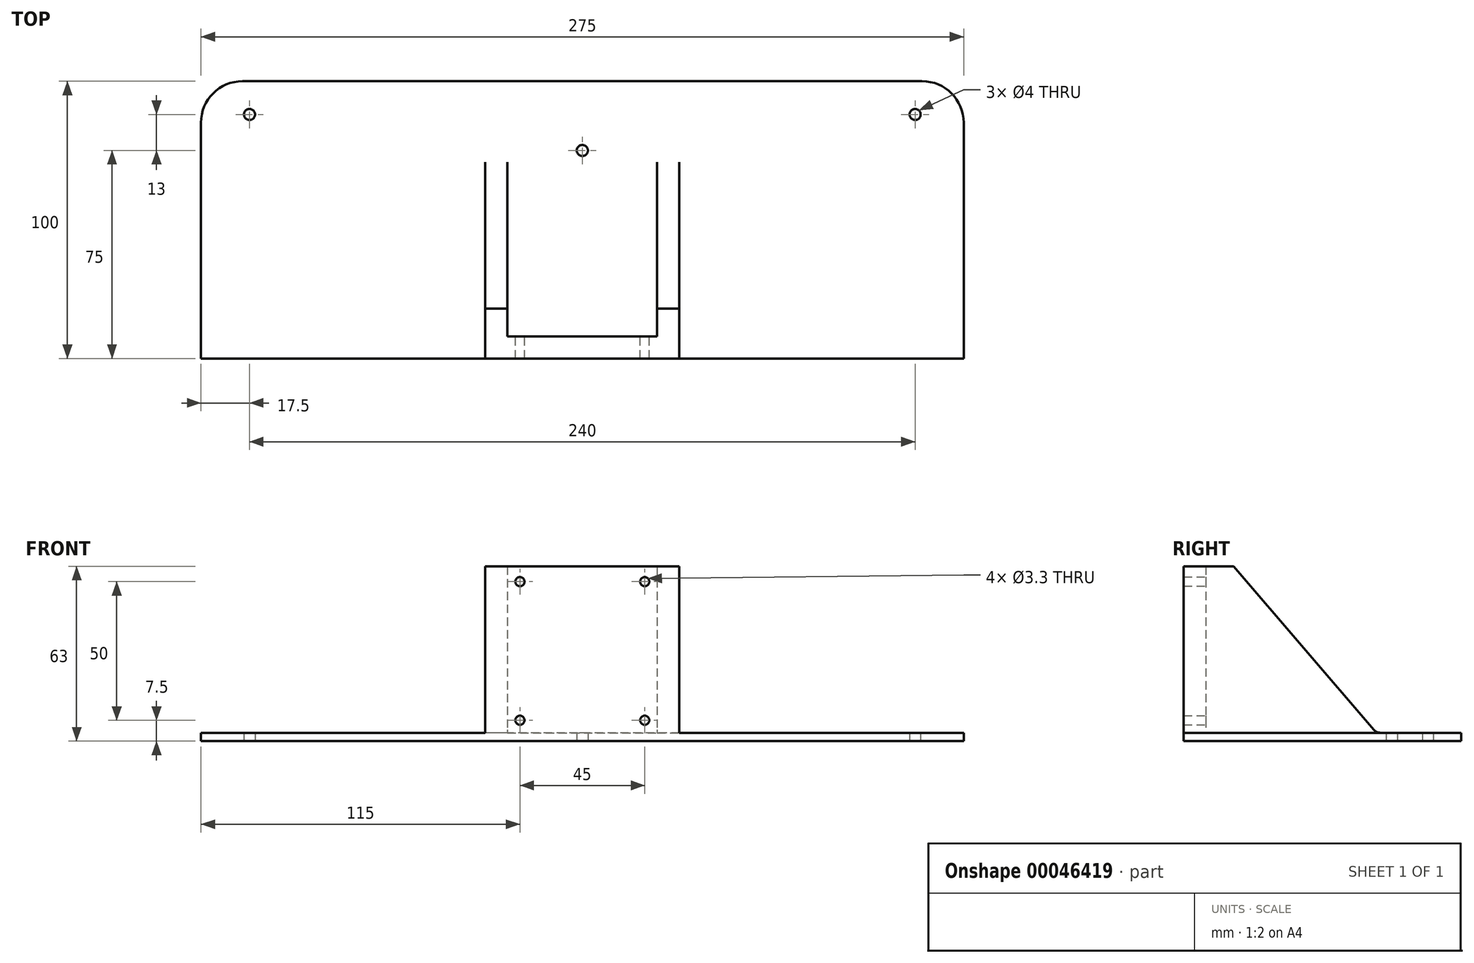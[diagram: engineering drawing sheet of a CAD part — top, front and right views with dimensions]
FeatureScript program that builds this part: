
annotation { "Feature Type Name" : "Feature", "Feature Type Description" : "" }
export const myFeature = defineFeature(function(context is Context, id is Id, definition is map)
    precondition{}
    {
        {
            var Q0;
            Q0=qCreatedBy(makeId("Top.planeOp"),FACE);
            var sketch = newSketch(context, id + "F0", { "sketchPlane" : qUnion([Q0])});
            skLineSegment(sketch, "E0.bottom", {"start": v(137.5, -50) * mm, "end": v(-137.5, -50) * mm});
            skLineSegment(sketch, "E0.top", {"start": v(122.5, 50) * mm, "end": v(-122.5, 50) * mm});
            skLineSegment(sketch, "E0.left", {"start": v(137.5, -50) * mm, "end": v(137.5, 35) * mm});
            skLineSegment(sketch, "E0.right", {"start": v(-137.5, -50) * mm, "end": v(-137.5, 35) * mm});
            skPoint(sketch, "E0.middle", {"position": v(0, 0) * mm});
            skPoint(sketch, "E1.visualSharp", {"position": v(-137.5, 50) * mm});
            skArc(sketch, "E1.filletArc", {"start": v(-122.5, 50) * mm, "mid": v(-133.1, 45.6) * mm, "end": v(-137.5, 35) * mm});
            skPoint(sketch, "E2.visualSharp", {"position": v(137.5, 50) * mm});
            skArc(sketch, "E2.filletArc", {"start": v(137.5, 35) * mm, "mid": v(133.1, 45.6) * mm, "end": v(122.5, 50) * mm});
            skPoint(sketch, "E3", {"position": v(0, 25) * mm});
            skPoint(sketch, "E4", {"position": v(-120, 38) * mm});
            skCircle(sketch, "E5", {"center": v(-120, 38) * mm, "radius": 2 * mm});
            skCircle(sketch, "E6", {"center": v(0, 25) * mm, "radius": 2 * mm});
            skCircle(sketch, "E7.MirrorC", {"center": v(120, 38) * mm, "radius": 2 * mm});
            skSolve(sketch);
        }
        {
            var Q0;
            Q0=makeQuery(id+"F0.imprint","IMPRINT",FACE,{"disambiguationData":[TD([[makeQuery(id+"F0.imprint","IMPRINT",EDGE,{"derivedFrom":sQuery(id+"F0.wireOp",EDGE,"E0.bottom")}),-1.0]])]});
            extrude(context, id + "F1", {"entities" : qUnion([Q0]), "depth" : 3 * mm, "offsetDistance" : 25 * mm});
        }
        {
            var Q0;
            Q0=makeQuery(id+"F1.opExtrude","CAP_FACE",FACE,{"disambiguationData":[OSD([sQuery(id+"F0.wireOp",EDGE,"E0.bottom"),sQuery(id+"F0.wireOp",EDGE,"E0.top"),sQuery(id+"F0.wireOp",EDGE,"E0.left"),sQuery(id+"F0.wireOp",EDGE,"E0.right"),sQuery(id+"F0.wireOp",EDGE,"E1.filletArc"),sQuery(id+"F0.wireOp",EDGE,"E2.filletArc"),sQuery(id+"F0.wireOp",EDGE,"E5"),sQuery(id+"F0.wireOp",EDGE,"E6"),sQuery(id+"F0.wireOp",EDGE,"E7.MirrorC")])],"isStart":false});
            var sketch = newSketch(context, id + "F2", { "sketchPlane" : qUnion([Q0])});
            skLineSegment(sketch, "E8.bottom", {"start": v(-35, -50) * mm, "end": v(35, -50) * mm});
            skLineSegment(sketch, "E8.top", {"start": v(-35, -42) * mm, "end": v(35, -42) * mm});
            skLineSegment(sketch, "E8.left", {"start": v(-35, -50) * mm, "end": v(-35, -42) * mm});
            skLineSegment(sketch, "E8.right", {"start": v(35, -50) * mm, "end": v(35, -42) * mm});
            skLineSegment(sketch, "E9.bottom", {"start": v(-35, -42) * mm, "end": v(-27, -42) * mm});
            skLineSegment(sketch, "E9.left", {"start": v(-35, -42) * mm, "end": v(-35, 28) * mm});
            skLineSegment(sketch, "E10.MirrorCS", {"start": v(35, -42) * mm, "end": v(35, 28) * mm});
            skLineSegment(sketch, "E11", {"start": v(-35, 28) * mm, "end": v(-27, 28) * mm});
            skLineSegment(sketch, "E12", {"start": v(-27, 28) * mm, "end": v(-27, -42) * mm});
            skLineSegment(sketch, "E13.MirrorCS", {"start": v(35, 28) * mm, "end": v(27, 28) * mm});
            skLineSegment(sketch, "E14.MirrorCS", {"start": v(27, 28) * mm, "end": v(27, -42) * mm});
            skSolve(sketch);
        }
        {
            var Q0;
            Q0=makeQuery(id+"F2.imprint","IMPRINT",FACE,{"disambiguationData":[TD([[makeQuery(id+"F2.imprint","IMPRINT",EDGE,{"derivedFrom":sQuery(id+"F2.wireOp",EDGE,"E8.bottom")}),-1.0]])]});
            var Q1;
            {var subQ2=sQuery(id+"F2.wireOp",EDGE,"E9.left");Q1=makeQuery(id+"F2.imprint","IMPRINT",FACE,{"disambiguationData":[TD([[makeQuery(id+"F2.imprint","IMPRINT",EDGE,{"derivedFrom":subQ2}),-1.0]])]});}
            var Q2;
            {var subQ0=sQuery(id+"F2.wireOp",EDGE,"E10.MirrorCS");Q2=makeQuery(id+"F2.imprint","IMPRINT",FACE,{"disambiguationData":[TD([[makeQuery(id+"F2.imprint","IMPRINT",EDGE,{"derivedFrom":subQ0}),1.0]])]});}
            extrude(context, id + "F3", {"entities" : qUnion([Q0, Q1, Q2]), "operationType" : NewBodyOperationType.ADD, "depth" : 60 * mm, "offsetDistance" : 25 * mm});
        }
        {
            var Q0;
            Q0=makeQuery(id+"F3.opExtrude","CAP_EDGE",EDGE,{"disambiguationData":[OSD([sQuery(id+"F2.wireOp",EDGE,"E11")])],"isStart":false});
            var Q1;
            Q1=makeQuery(id+"F3.opExtrude","CAP_EDGE",EDGE,{"disambiguationData":[OSD([sQuery(id+"F2.wireOp",EDGE,"E13.MirrorCS")])],"isStart":false});
            chamfer(context, id + "F4", {"entities" : qUnion([Q0, Q1]), "chamferType" : ChamferType.TWO_OFFSETS, "width1" : 60 * mm, "oppositeDirection" : false, "width2" : 70 * mm, "tangentPropagation" : true});
        }
        {
            var Q0;
            Q0=makeQuery(id+"F3.opExtrude","CAP_EDGE",EDGE,{"disambiguationData":[OSD([sQuery(id+"F2.wireOp",EDGE,"E8.right"),sQuery(id+"F2.wireOp",EDGE,"E10.MirrorCS")])],"isStart":true});
            var Q1;
            Q1=makeQuery(id+"F3.opExtrude","CAP_EDGE",EDGE,{"disambiguationData":[OSD([sQuery(id+"F2.wireOp",EDGE,"E8.left"),sQuery(id+"F2.wireOp",EDGE,"E9.left")])],"isStart":true});
            var Q2;
            Q2=makeQuery(id+"F3.opExtrude","CAP_EDGE",EDGE,{"disambiguationData":[OSD([sQuery(id+"F2.wireOp",EDGE,"E12")])],"isStart":true});
            var Q3;
            Q3=makeQuery(id+"F3.opExtrude","CAP_EDGE",EDGE,{"disambiguationData":[OSD([sQuery(id+"F2.wireOp",EDGE,"E8.top")])],"isStart":true});
            var Q4;
            Q4=makeQuery(id+"F3.opExtrude","CAP_EDGE",EDGE,{"disambiguationData":[OSD([sQuery(id+"F2.wireOp",EDGE,"E14.MirrorCS")])],"isStart":true});
            var Q5;
            Q5=makeQuery(id+"F4.opChamfer","BLEND_EDGE",EDGE,{"blendedFrom":[makeQuery(id+"F3.opExtrude","CAP_EDGE",EDGE,{"disambiguationData":[OSD([sQuery(id+"F2.wireOp",EDGE,"E11")])],"isStart":false}),makeQuery(id+"F1.opExtrude","CAP_FACE",FACE,{"disambiguationData":[OSD([sQuery(id+"F0.wireOp",EDGE,"E0.bottom"),sQuery(id+"F0.wireOp",EDGE,"E0.top"),sQuery(id+"F0.wireOp",EDGE,"E0.left"),sQuery(id+"F0.wireOp",EDGE,"E0.right"),sQuery(id+"F0.wireOp",EDGE,"E1.filletArc"),sQuery(id+"F0.wireOp",EDGE,"E2.filletArc"),sQuery(id+"F0.wireOp",EDGE,"E5"),sQuery(id+"F0.wireOp",EDGE,"E6"),sQuery(id+"F0.wireOp",EDGE,"E7.MirrorC")])],"isStart":false})],"blendedInto":[makeQuery(id+"F1.opExtrude","CAP_FACE",FACE,{"disambiguationData":[OSD([sQuery(id+"F0.wireOp",EDGE,"E0.bottom"),sQuery(id+"F0.wireOp",EDGE,"E0.top"),sQuery(id+"F0.wireOp",EDGE,"E0.left"),sQuery(id+"F0.wireOp",EDGE,"E0.right"),sQuery(id+"F0.wireOp",EDGE,"E1.filletArc"),sQuery(id+"F0.wireOp",EDGE,"E2.filletArc"),sQuery(id+"F0.wireOp",EDGE,"E5"),sQuery(id+"F0.wireOp",EDGE,"E6"),sQuery(id+"F0.wireOp",EDGE,"E7.MirrorC")])],"isStart":false})]});
            var Q6;
            Q6=makeQuery(id+"F4.opChamfer","BLEND_EDGE",EDGE,{"blendedFrom":[makeQuery(id+"F3.opExtrude","CAP_EDGE",EDGE,{"disambiguationData":[OSD([sQuery(id+"F2.wireOp",EDGE,"E13.MirrorCS")])],"isStart":false}),makeQuery(id+"F1.opExtrude","CAP_FACE",FACE,{"disambiguationData":[OSD([sQuery(id+"F0.wireOp",EDGE,"E0.bottom"),sQuery(id+"F0.wireOp",EDGE,"E0.top"),sQuery(id+"F0.wireOp",EDGE,"E0.left"),sQuery(id+"F0.wireOp",EDGE,"E0.right"),sQuery(id+"F0.wireOp",EDGE,"E1.filletArc"),sQuery(id+"F0.wireOp",EDGE,"E2.filletArc"),sQuery(id+"F0.wireOp",EDGE,"E5"),sQuery(id+"F0.wireOp",EDGE,"E6"),sQuery(id+"F0.wireOp",EDGE,"E7.MirrorC")])],"isStart":false})],"blendedInto":[makeQuery(id+"F1.opExtrude","CAP_FACE",FACE,{"disambiguationData":[OSD([sQuery(id+"F0.wireOp",EDGE,"E0.bottom"),sQuery(id+"F0.wireOp",EDGE,"E0.top"),sQuery(id+"F0.wireOp",EDGE,"E0.left"),sQuery(id+"F0.wireOp",EDGE,"E0.right"),sQuery(id+"F0.wireOp",EDGE,"E1.filletArc"),sQuery(id+"F0.wireOp",EDGE,"E2.filletArc"),sQuery(id+"F0.wireOp",EDGE,"E5"),sQuery(id+"F0.wireOp",EDGE,"E6"),sQuery(id+"F0.wireOp",EDGE,"E7.MirrorC")])],"isStart":false})]});
            fillet(context, id + "F5", {"entities" : qUnion([Q0, Q1, Q2, Q3, Q4, Q5, Q6]), "radius" : 3 * mm, "tangentPropagation" : true, "allowEdgeOverflow" : false});
        }
        {
            var Q0;
            Q0=makeQuery(id+"F3.boolean.opBoolean","MERGE",FACE,{"derivedFrom":[makeQuery(id+"F1.opExtrude","SWEPT_FACE",FACE,{"disambiguationData":[OSD([sQuery(id+"F0.wireOp",EDGE,"E0.bottom")])]}),makeQuery(id+"F3.opExtrude","SWEPT_FACE",FACE,{"disambiguationData":[OSD([sQuery(id+"F2.wireOp",EDGE,"E8.bottom")])]})]});
            var sketch = newSketch(context, id + "F6", { "sketchPlane" : qUnion([Q0])});
            skPoint(sketch, "E15", {"position": v(-22.5, 57.5) * mm});
            skPoint(sketch, "E16", {"position": v(-22.5, 7.5) * mm});
            skPoint(sketch, "E17.MirrorP", {"position": v(22.5, 57.5) * mm});
            skPoint(sketch, "E18.MirrorP", {"position": v(22.5, 7.5) * mm});
            skSolve(sketch);
        }
        {
            var Q0;
            Q0=sQuery(id+"F6.wireOp",VERTEX,"E15");
            var Q1;
            Q1=sQuery(id+"F6.wireOp",VERTEX,"E17.MirrorP");
            var Q2;
            Q2=sQuery(id+"F6.wireOp",VERTEX,"E16");
            var Q3;
            Q3=sQuery(id+"F6.wireOp",VERTEX,"E18.MirrorP");
            var Q4;
            Q4=makeQuery(id+"F1.opExtrude","SWEPT_BODY",BODY,{"disambiguationData":[OSD([sQuery(id+"F0.wireOp",EDGE,"E0.bottom"),sQuery(id+"F0.wireOp",EDGE,"E0.top"),sQuery(id+"F0.wireOp",EDGE,"E0.left"),sQuery(id+"F0.wireOp",EDGE,"E0.right"),sQuery(id+"F0.wireOp",EDGE,"E1.filletArc"),sQuery(id+"F0.wireOp",EDGE,"E2.filletArc"),sQuery(id+"F0.wireOp",EDGE,"E5"),sQuery(id+"F0.wireOp",EDGE,"E6"),sQuery(id+"F0.wireOp",EDGE,"E7.MirrorC")])]});
            hole(context, id + "F7", {"style" : HoleStyle.SIMPLE, "endStyle" : HoleEndStyle.BLIND, "standardTappedOrClearance" : lookupTablePath({ "standard" : "ISO", "engagement" : "75%", "pitch" : "0.7 mm", "size" : "M4", "type" : "Tapped" }), "standardBlindInLast" : lookupTablePath({ "standard" : "ISO", "engagement" : "75%", "pitch" : "0.7 mm", "size" : "M4", "type" : "Tapped" }), "holeDiameter" : 3.3 * mm, "majorDiameter" : 4 * mm, "showTappedDepth" : true, "holeDepth" : 14.1 * mm, "tappedDepth" : 12 * mm, "tapClearance" : 3, "locations" : qUnion([Q0, Q1, Q2, Q3]), "scope" : qUnion([Q4]), "startStyle" : HoleStartStyle.PART});
        }
    });
